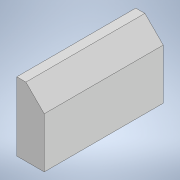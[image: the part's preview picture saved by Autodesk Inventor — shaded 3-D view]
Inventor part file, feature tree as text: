
AUTODESK INVENTOR PART (.ipt)
format: ipt  version: 2021 (Build 250183000, 183)  size: 89,088 bytes
history: native  units: in
note: dims shown in document units (in); Inventor stores cm internally (conversion verified against a paired STEP export)
features: extrude x1, sketch x1
ambient origin geometry x8: Origin, YZ Plane, XZ Plane, XY Plane, X Axis, Y Axis, Z Axis, Center Point
bodies: Solid1 (feature_tree)
feature tree (2):
  extrude  "Extrusion1"  Depth=1.0236in
  sketch  "Sketch1"  dims[d0=0.2362in d1=0.4331in d2=0.5906in d3=0.0787in d4=1.0236in d5=0.0in]
